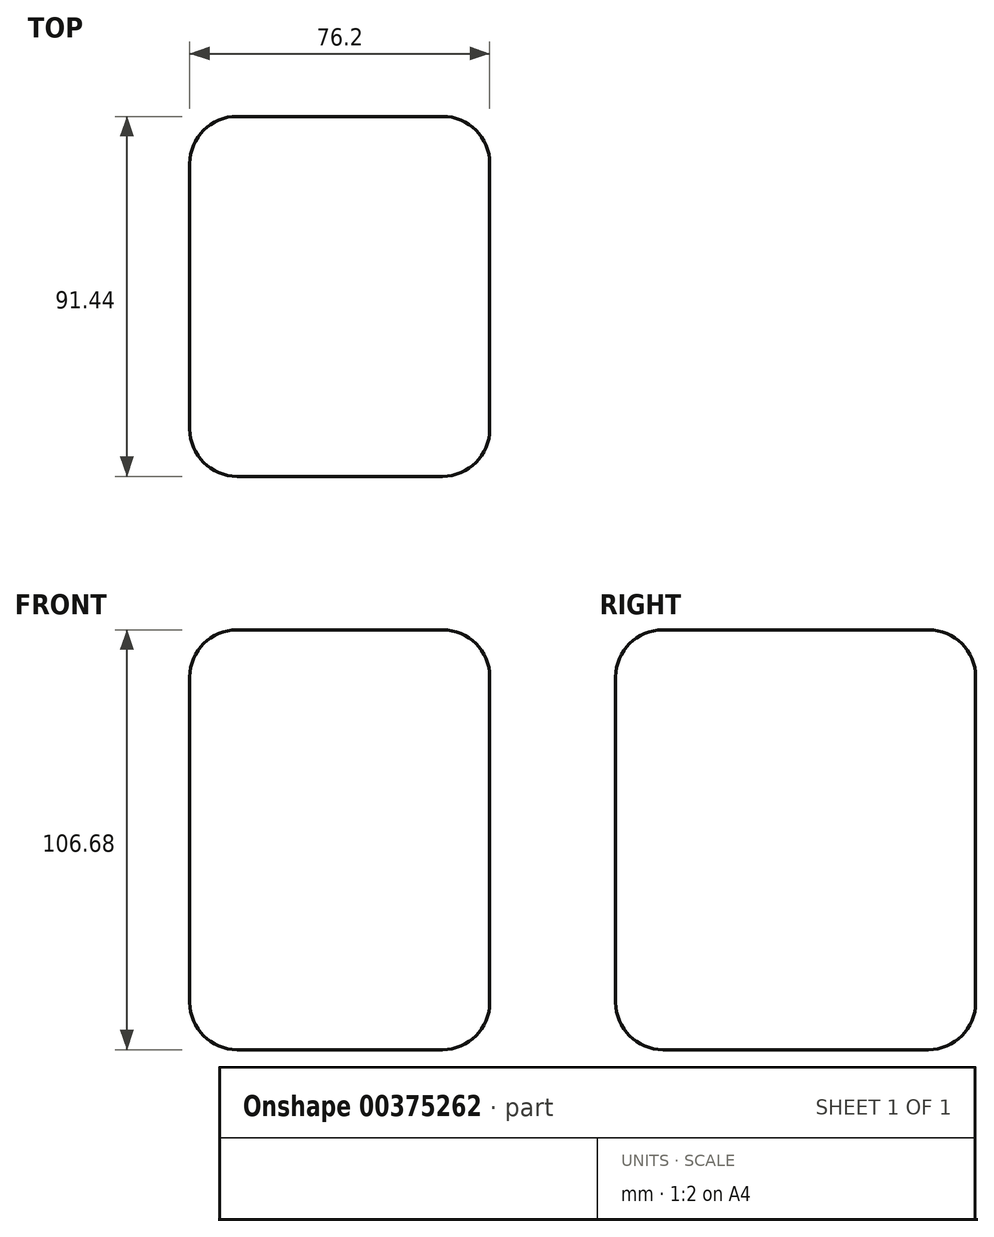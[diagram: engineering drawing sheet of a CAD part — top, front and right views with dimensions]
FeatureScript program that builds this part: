
annotation { "Feature Type Name" : "Feature", "Feature Type Description" : "" }
export const myFeature = defineFeature(function(context is Context, id is Id, definition is map)
    precondition{}
    {
        {
            var Q0;
            Q0=qCreatedBy(makeId("Top.planeOp"),FACE);
            var sketch = newSketch(context, id + "F0", { "sketchPlane" : qUnion([Q0])});
            skLineSegment(sketch, "E0.bottom", {"start": v(-38.1, 45.72) * mm, "end": v(38.1, 45.72) * mm});
            skLineSegment(sketch, "E0.top", {"start": v(-38.1, -45.72) * mm, "end": v(38.1, -45.72) * mm});
            skLineSegment(sketch, "E0.left", {"start": v(-38.1, 45.72) * mm, "end": v(-38.1, -45.72) * mm});
            skLineSegment(sketch, "E0.right", {"start": v(38.1, 45.72) * mm, "end": v(38.1, -45.72) * mm});
            skSolve(sketch);
        }
        {
            var Q0;
            Q0=makeQuery(id+"F0.imprint","IMPRINT",FACE,{"disambiguationData":[TD([[makeQuery(id+"F0.imprint","IMPRINT",EDGE,{"derivedFrom":sQuery(id+"F0.wireOp",EDGE,"E0.bottom")}),-1.0]])]});
            extrude(context, id + "F1", {"entities" : qUnion([Q0]), "depth" : 106.68 * mm});
        }
        {
            var Q0;
            Q0=makeQuery(id+"F1.opExtrude","SWEPT_FACE",FACE,{"disambiguationData":[OSD([sQuery(id+"F0.wireOp",EDGE,"E0.left")])]});
            var Q1;
            Q1=makeQuery(id+"F1.opExtrude","CAP_EDGE",EDGE,{"disambiguationData":[OSD([sQuery(id+"F0.wireOp",EDGE,"E0.top")])],"isStart":false});
            var Q2;
            Q2=makeQuery(id+"F1.opExtrude","CAP_EDGE",EDGE,{"disambiguationData":[OSD([sQuery(id+"F0.wireOp",EDGE,"E0.right")])],"isStart":false});
            var Q3;
            Q3=makeQuery(id+"F1.opExtrude","CAP_FACE",FACE,{"disambiguationData":[OSD([sQuery(id+"F0.wireOp",EDGE,"E0.bottom"),sQuery(id+"F0.wireOp",EDGE,"E0.top"),sQuery(id+"F0.wireOp",EDGE,"E0.left"),sQuery(id+"F0.wireOp",EDGE,"E0.right")])],"isStart":false});
            var Q4;
            Q4=makeQuery(id+"F1.opExtrude","CAP_EDGE",EDGE,{"disambiguationData":[OSD([sQuery(id+"F0.wireOp",EDGE,"E0.top")])],"isStart":true});
            var Q5;
            Q5=makeQuery(id+"F1.opExtrude","SWEPT_EDGE",EDGE,{"disambiguationData":[OSD([sQuery(id+"F0.wireOp",EDGE,"E0.top"),sQuery(id+"F0.wireOp",EDGE,"E0.right")])]});
            var Q6;
            Q6=makeQuery(id+"F1.opExtrude","CAP_EDGE",EDGE,{"disambiguationData":[OSD([sQuery(id+"F0.wireOp",EDGE,"E0.right")])],"isStart":true});
            var Q7;
            Q7=makeQuery(id+"F1.opExtrude","SWEPT_EDGE",EDGE,{"disambiguationData":[OSD([sQuery(id+"F0.wireOp",EDGE,"E0.bottom"),sQuery(id+"F0.wireOp",EDGE,"E0.right")])]});
            var Q8;
            Q8=makeQuery(id+"F1.opExtrude","CAP_EDGE",EDGE,{"disambiguationData":[OSD([sQuery(id+"F0.wireOp",EDGE,"E0.bottom")])],"isStart":true});
            fillet(context, id + "F2", {"entities" : qUnion([Q0, Q1, Q2, Q3, Q4, Q5, Q6, Q7, Q8]), "radius" : 12 * mm, "tangentPropagation" : true, "allowEdgeOverflow" : false});
        }
    });
